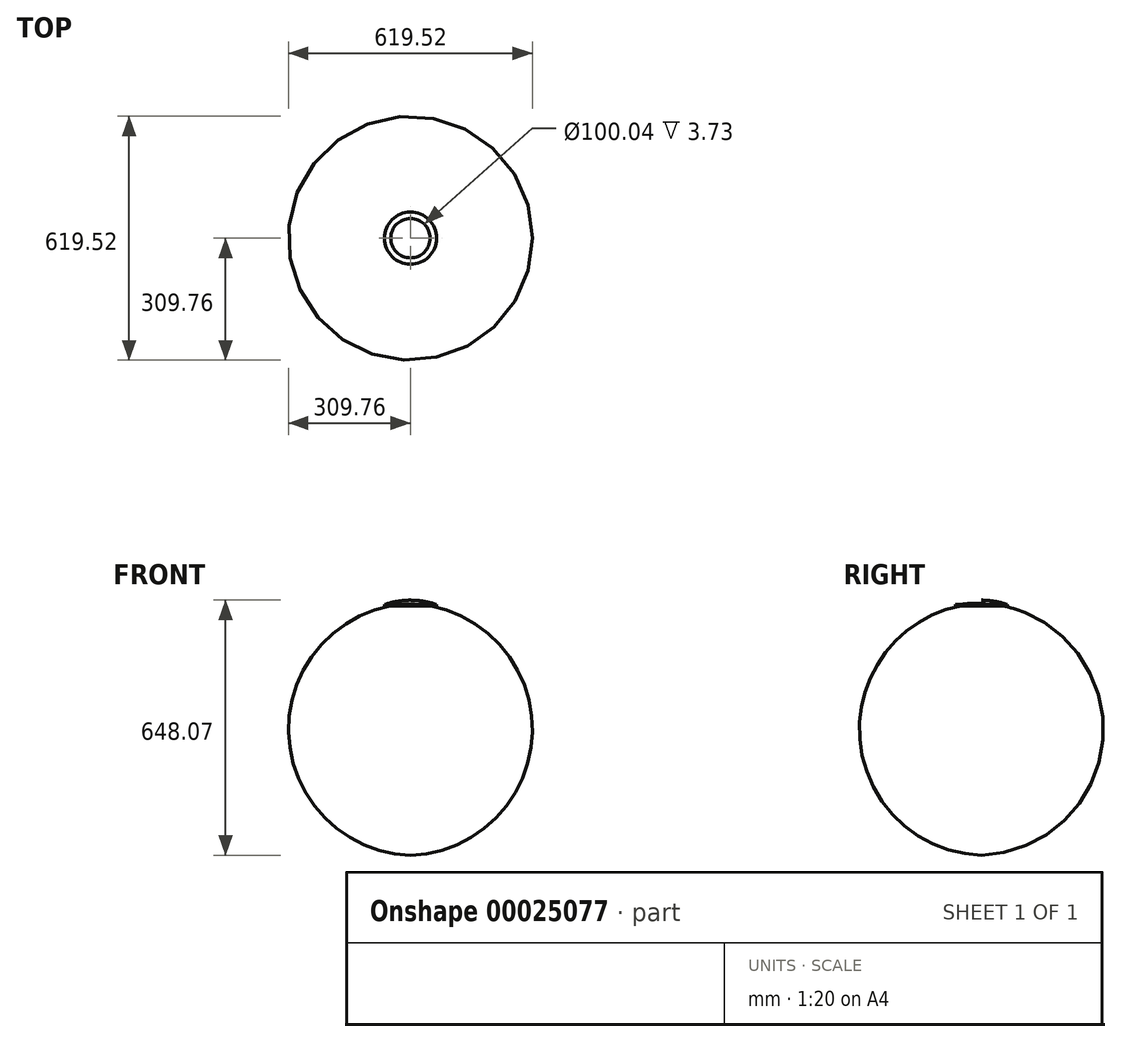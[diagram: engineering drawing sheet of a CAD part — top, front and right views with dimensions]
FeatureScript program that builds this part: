
annotation { "Feature Type Name" : "Feature", "Feature Type Description" : "" }
export const myFeature = defineFeature(function(context is Context, id is Id, definition is map)
    precondition{}
    {
        {
            var Q0;
            Q0=qCreatedBy(makeId("Front.planeOp"),FACE);
            var sketch = newSketch(context, id + "F0", { "sketchPlane" : qUnion([Q0])});
            skLineSegment(sketch, "E0", {"start": v(50.02, 0) * mm, "end": v(66.32, 0) * mm});
            skLineSegment(sketch, "E1", {"start": v(66.32, 0) * mm, "end": v(66.32, 2.9) * mm});
            skLineSegment(sketch, "E2", {"start": v(50.02, 0) * mm, "end": v(50.02, 3.73) * mm});
            skArc(sketch, "E3", {"start": v(66.32, 2.9) * mm, "mid": v(33.62, 11.22) * mm, "end": v(0, 14.18) * mm});
            skArc(sketch, "E4", {"start": v(50.02, 3.73) * mm, "mid": v(25.06, 5.86) * mm, "end": v(0, 6.03) * mm});
            skLineSegment(sketch, "E5", {"start": v(0, 6.03) * mm, "end": v(0, 14.18) * mm});
            skSolve(sketch);
        }
        {
            var Q0;
            Q0 = qSketchRegion(id + "F0", true);
            var Q1;
            Q1=sQuery(id+"F0.wireOp",EDGE,"E5");
            revolve(context, id + "F1", {"entities" : qUnion([Q0]), "axis" : qUnion([Q1]), "revolveType" : RevolveType.FULL});
        }
    });
